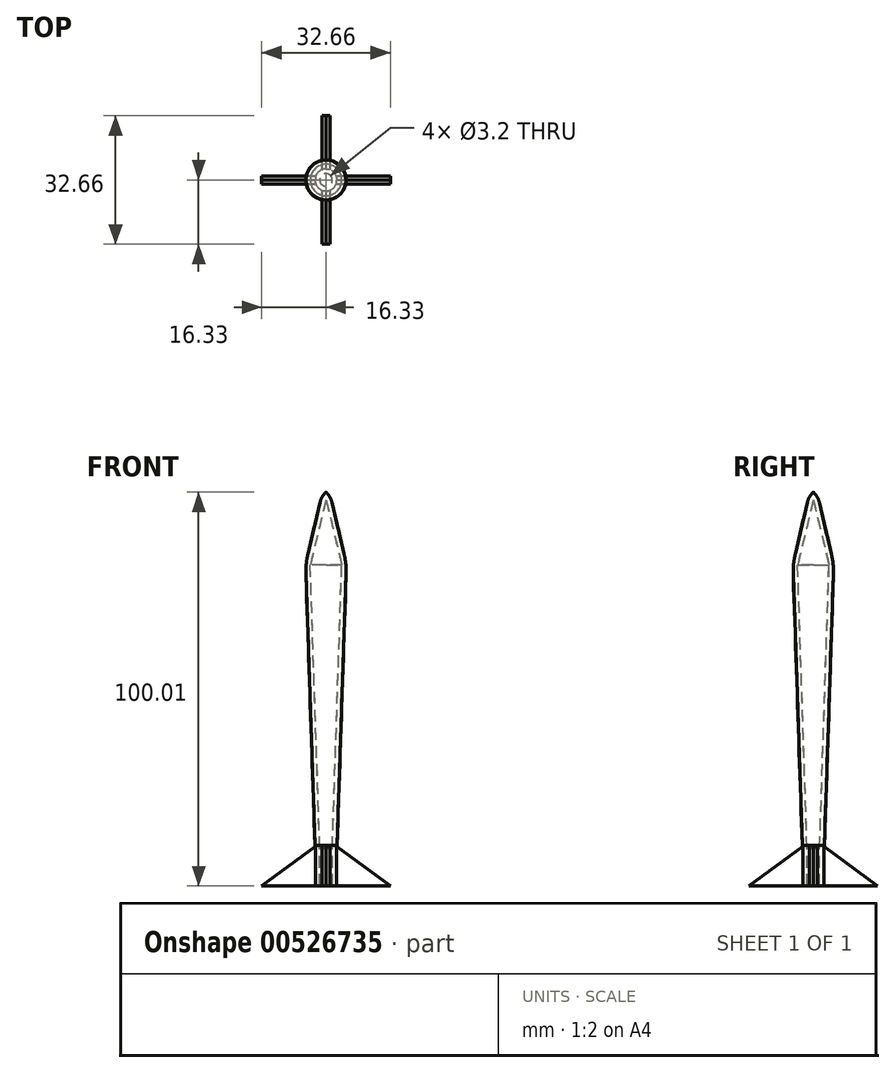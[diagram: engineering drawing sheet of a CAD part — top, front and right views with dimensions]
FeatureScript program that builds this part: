
annotation { "Feature Type Name" : "Feature", "Feature Type Description" : "" }
export const myFeature = defineFeature(function(context is Context, id is Id, definition is map)
    precondition{}
    {
        {
            var Q0;
            Q0=qCreatedBy(makeId("Front.planeOp"),FACE);
            var sketch = newSketch(context, id + "F0", { "sketchPlane" : qUnion([Q0])});
            skLineSegment(sketch, "E0", {"start": v(0, 29.06) * mm, "end": v(0, 27.06) * mm});
            skLineSegment(sketch, "E1", {"start": v(-4, 10.62) * mm, "end": v(-1.6, -61.43) * mm});
            skLineSegment(sketch, "E2", {"start": v(-1.6, -61.43) * mm, "end": v(-1.6, -70.94) * mm});
            skLineSegment(sketch, "E3", {"start": v(-5.19, 10.8) * mm, "end": v(-1.18, 27.94) * mm});
            skLineSegment(sketch, "E4", {"start": v(-1.18, 27.94) * mm, "end": v(0, 29.06) * mm});
            skLineSegment(sketch, "E5", {"start": v(-4, 10.62) * mm, "end": v(0, 27.06) * mm});
            skLineSegment(sketch, "E6", {"start": v(-5.19, 10.8) * mm, "end": v(-2.8, -60.73) * mm});
            skLineSegment(sketch, "E7", {"start": v(-2.8, -60.73) * mm, "end": v(-2.8, -70.95) * mm});
            skLineSegment(sketch, "E8", {"start": v(-2.8, -70.95) * mm, "end": v(-1.6, -70.94) * mm});
            skSolve(sketch);
        }
        {
            var Q0;
            Q0=makeQuery(id+"F0.imprint","IMPRINT",FACE,{"disambiguationData":[TD([[makeQuery(id+"F0.imprint","IMPRINT",EDGE,{"derivedFrom":sQuery(id+"F0.wireOp",EDGE,"E0")}),-1.0]])]});
            var Q1;
            Q1=sQuery(id+"F0.wireOp",EDGE,"E0");
            revolve(context, id + "F1", {"entities" : qUnion([Q0]), "axis" : qUnion([Q1]), "revolveType" : RevolveType.FULL});
        }
        {
            var Q0;
            Q0=makeQuery(id+"F1.opRevolve","SWEPT_EDGE",EDGE,{"disambiguationData":[OSD([sQuery(id+"F0.wireOp",EDGE,"E3"),sQuery(id+"F0.wireOp",EDGE,"E6")])]});
            fillet(context, id + "F2", {"entities" : qUnion([Q0]), "radius" : 20 * mm, "tangentPropagation" : true, "allowEdgeOverflow" : false});
        }
        {
            var Q0;
            Q0=makeQuery(id+"F1.opRevolve","SWEPT_EDGE",EDGE,{"disambiguationData":[OSD([sQuery(id+"F0.wireOp",EDGE,"E3"),sQuery(id+"F0.wireOp",EDGE,"E4")])]});
            fillet(context, id + "F3", {"entities" : qUnion([Q0]), "radius" : 5 * mm, "tangentPropagation" : true, "allowEdgeOverflow" : false});
        }
        {
            var Q0;
            Q0=qCreatedBy(makeId("Front.planeOp"),FACE);
            var sketch = newSketch(context, id + "F4", { "sketchPlane" : qUnion([Q0])});
            skLineSegment(sketch, "E9", {"start": v(-2.67, -60.91) * mm, "end": v(-2.67, -70.91) * mm});
            skLineSegment(sketch, "E10", {"start": v(-2.67, -70.91) * mm, "end": v(-16.33, -70.91) * mm});
            skLineSegment(sketch, "E11", {"start": v(-16.33, -70.91) * mm, "end": v(-2.67, -60.91) * mm});
            skLineSegment(sketch, "E12", {"start": v(0, -60.83) * mm, "end": v(0, -70.98) * mm});
            skSolve(sketch);
        }
        {
            var Q0;
            Q0=makeQuery(id+"F4.imprint","IMPRINT",FACE,{"disambiguationData":[TD([[makeQuery(id+"F4.imprint","IMPRINT",EDGE,{"derivedFrom":sQuery(id+"F4.wireOp",EDGE,"E9")}),-1.0]])]});
            extrude(context, id + "F5", {"entities" : qUnion([Q0]), "operationType" : NewBodyOperationType.ADD, "depth" : 1 * mm, "offsetDistance" : 25 * mm});
        }
        {
            var Q0;
            Q0 = qSketchRegion(id + "F4", true);
            extrude(context, id + "F6", {"entities" : qUnion([Q0]), "oppositeDirection" : true, "depth" : 1 * mm, "offsetDistance" : 25 * mm});
        }
        {
            var Q0;
            Q0=makeQuery(id+"F1.opRevolve","SWEPT_BODY",BODY,{"disambiguationData":[OSD([sQuery(id+"F0.wireOp",EDGE,"E0"),sQuery(id+"F0.wireOp",EDGE,"E1"),sQuery(id+"F0.wireOp",EDGE,"E2"),sQuery(id+"F0.wireOp",EDGE,"E3"),sQuery(id+"F0.wireOp",EDGE,"E4"),sQuery(id+"F0.wireOp",EDGE,"E5"),sQuery(id+"F0.wireOp",EDGE,"E6"),sQuery(id+"F0.wireOp",EDGE,"E7"),sQuery(id+"F0.wireOp",EDGE,"E8")])]});
            var Q1;
            Q1=makeQuery(id+"F6.opExtrude","SWEPT_BODY",BODY,{"disambiguationData":[OSD([sQuery(id+"F4.wireOp",EDGE,"E9"),sQuery(id+"F4.wireOp",EDGE,"E10"),sQuery(id+"F4.wireOp",EDGE,"E11")])]});
            var Q2;
            Q2=sQuery(id+"F4.wireOp",EDGE,"E12");
            circularPattern(context, id + "F7", {"entities" : qUnion([Q0, Q1]), "axis" : qUnion([Q2]), "angle" : 360 * degree, "instanceCount" : 4, "equalSpace" : true});
        }
    });
